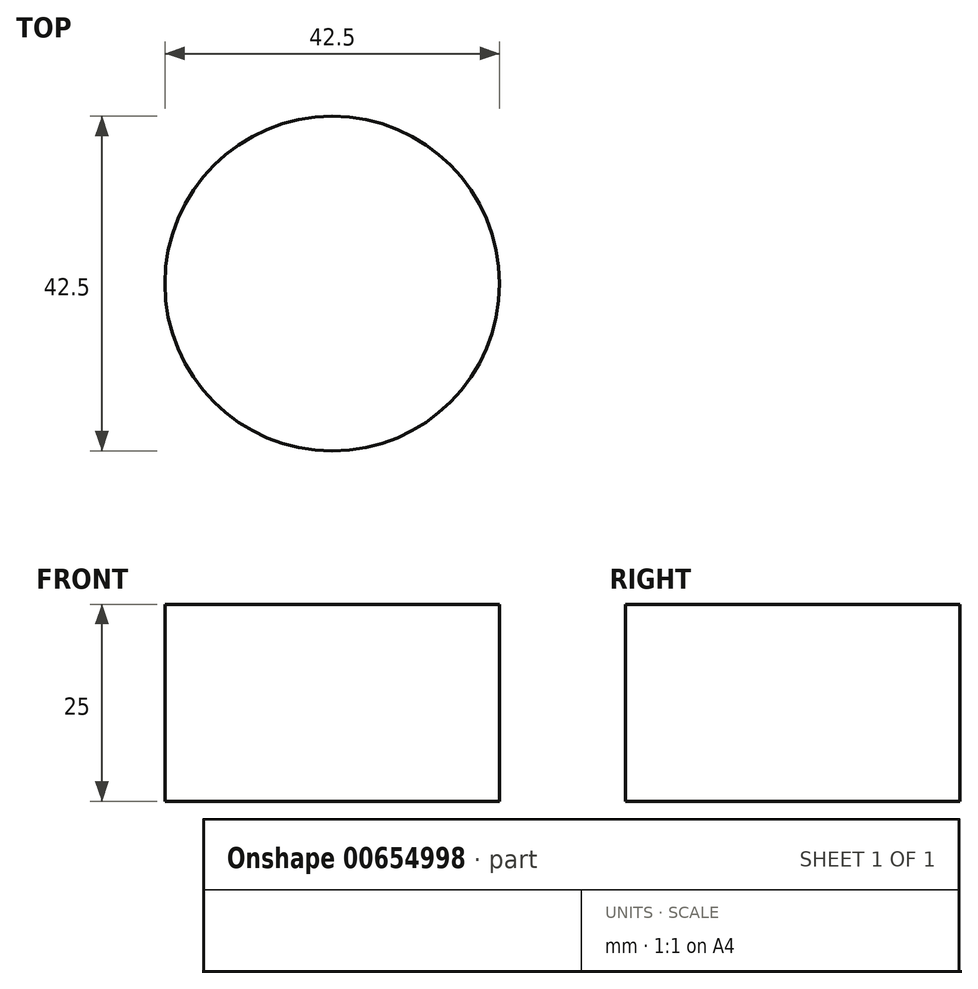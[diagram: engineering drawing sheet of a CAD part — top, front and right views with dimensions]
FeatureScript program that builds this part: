
annotation { "Feature Type Name" : "Feature", "Feature Type Description" : "" }
export const myFeature = defineFeature(function(context is Context, id is Id, definition is map)
    precondition{}
    {
        {
            var Q0;
            Q0=qCreatedBy(makeId("Top.planeOp"),FACE);
            var sketch = newSketch(context, id + "F0", { "sketchPlane" : qUnion([Q0])});
            skCircle(sketch, "E0", {"center": v(0, 0) * mm, "radius": 21.25 * mm});
            skSolve(sketch);
        }
        {
            var Q0;
            Q0 = qSketchRegion(id + "F0", true);
            extrude(context, id + "F1", {"entities" : qUnion([Q0]), "depth" : 25 * mm, "offsetDistance" : 25 * mm});
        }
        {
            var Q0;
            Q0=qCreatedBy(makeId("Right.planeOp"),FACE);
            var sketch = newSketch(context, id + "F2", { "sketchPlane" : qUnion([Q0])});
            skLineSegment(sketch, "E1.bottom", {"start": v(138.16, -12.16) * mm, "end": v(248.68, -12.16) * mm});
            skLineSegment(sketch, "E1.top", {"start": v(138.16, -105.49) * mm, "end": v(248.68, -105.49) * mm});
            skLineSegment(sketch, "E1.left", {"start": v(138.16, -12.16) * mm, "end": v(138.16, -105.49) * mm});
            skLineSegment(sketch, "E1.right", {"start": v(248.68, -12.16) * mm, "end": v(248.68, -105.49) * mm});
            skSolve(sketch);
        }
        {
            var Q0;
            Q0 = qSketchRegion(id + "F2", true);
            var Q1;
            Q1=sQuery(id+"F2.wireOp",EDGE,"E1.bottom");
            extrude(context, id + "F3", {"entities" : qUnion([Q0]), "bodyType" : ToolBodyType.SURFACE, "surfaceEntities" : qUnion([Q1]), "depth" : 25 * mm, "offsetDistance" : 25 * mm});
        }
    });
